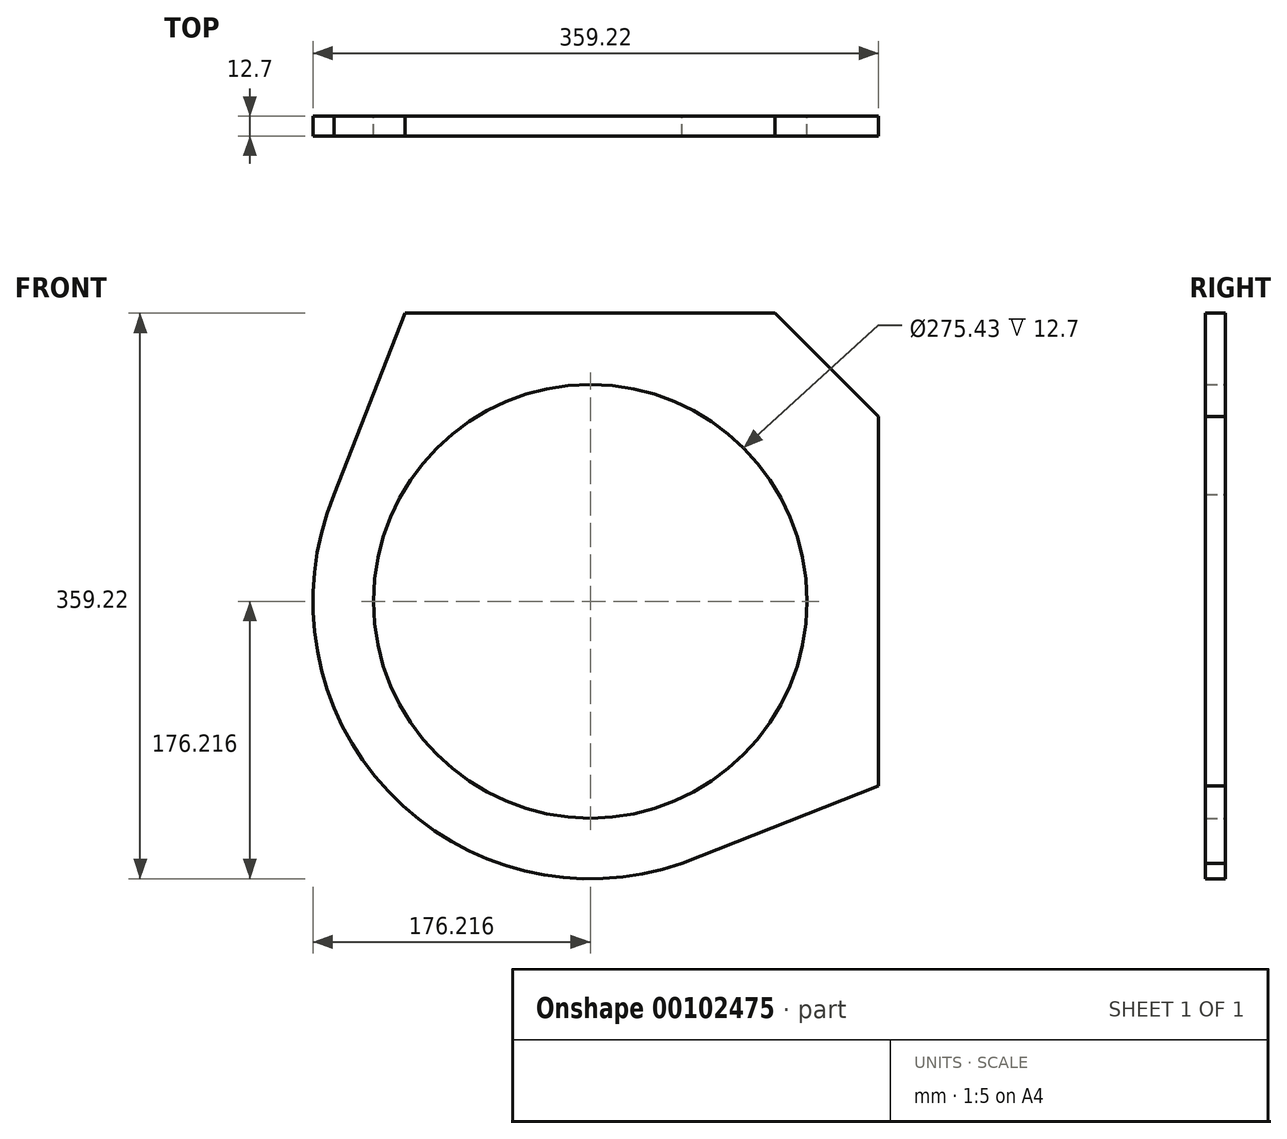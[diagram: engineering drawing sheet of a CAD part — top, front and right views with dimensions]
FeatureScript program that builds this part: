
annotation { "Feature Type Name" : "Feature", "Feature Type Description" : "" }
export const myFeature = defineFeature(function(context is Context, id is Id, definition is map)
    precondition{}
    {
        {
            var Q0;
            Q0=qCreatedBy(makeId("Front.planeOp"),FACE);
            var sketch = newSketch(context, id + "F0", { "sketchPlane" : qUnion([Q0])});
            skLineSegment(sketch, "E0", {"start": v(-121.07, 179.6) * mm, "end": v(-166.03, 64.44) * mm});
            skLineSegment(sketch, "E1", {"start": v(179.6, -120.62) * mm, "end": v(54.74, -169.74) * mm});
            skLineSegment(sketch, "E2", {"start": v(113.93, 179.6) * mm, "end": v(179.6, 114.02) * mm});
            skLineSegment(sketch, "E3", {"start": v(179.6, 114.02) * mm, "end": v(179.6, -120.62) * mm});
            skLineSegment(sketch, "E4", {"start": v(113.93, 179.6) * mm, "end": v(-121.07, 179.6) * mm});
            skArc(sketch, "E5", {"start": v(-166.03, 64.44) * mm, "mid": v(-131.61, -124.27) * mm, "end": v(54.74, -169.74) * mm});
            skCircle(sketch, "E6", {"center": v(-3.4, -3.4) * mm, "radius": 137.72 * mm});
            skSolve(sketch);
        }
        {
            var Q0;
            Q0 = qSketchRegion(id + "F0", true);
            extrude(context, id + "F1", {"entities" : qUnion([Q0]), "depth" : 12.7 * mm});
        }
    });
